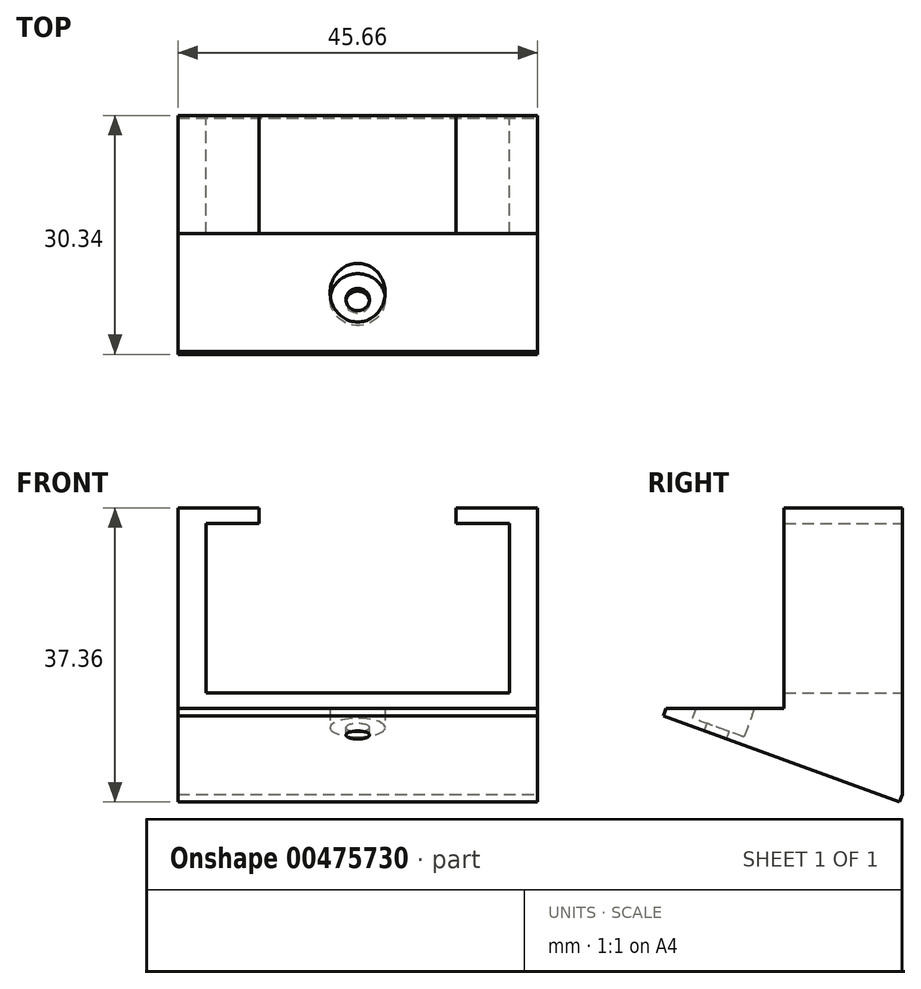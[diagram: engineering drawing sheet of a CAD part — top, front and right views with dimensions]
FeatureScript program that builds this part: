
annotation { "Feature Type Name" : "Feature", "Feature Type Description" : "" }
export const myFeature = defineFeature(function(context is Context, id is Id, definition is map)
    precondition{}
    {
        {
            var Q0;
            Q0=qCreatedBy(makeId("Front.planeOp"),FACE);
            var sketch = newSketch(context, id + "F0", { "sketchPlane" : qUnion([Q0])});
            skLineSegment(sketch, "E0.bottom", {"start": v(-19.25, 0) * mm, "end": v(19.25, 0) * mm});
            skLineSegment(sketch, "E0.top", {"start": v(-19.25, 21.5) * mm, "end": v(19.25, 21.5) * mm});
            skLineSegment(sketch, "E0.left", {"start": v(-19.25, 0) * mm, "end": v(-19.25, 21.5) * mm});
            skLineSegment(sketch, "E0.right", {"start": v(19.25, 0) * mm, "end": v(19.25, 21.5) * mm});
            skLineSegment(sketch, "E1.bottom", {"start": v(-22.83, -2) * mm, "end": v(22.83, -2) * mm});
            skLineSegment(sketch, "E1.top", {"start": v(-22.83, 23.5) * mm, "end": v(22.83, 23.5) * mm});
            skLineSegment(sketch, "E1.left", {"start": v(-22.83, -2) * mm, "end": v(-22.83, 23.5) * mm});
            skLineSegment(sketch, "E1.right", {"start": v(22.83, -2) * mm, "end": v(22.83, 23.5) * mm});
            skLineSegment(sketch, "E2", {"start": v(19.25, 21.5) * mm, "end": v(22.83, 23.5) * mm, "construction": true});
            skLineSegment(sketch, "E3", {"start": v(-19.25, 0) * mm, "end": v(-22.83, -2) * mm, "construction": true});
            skLineSegment(sketch, "E4", {"start": v(-12.5, 23.5) * mm, "end": v(-12.5, 21.5) * mm});
            skLineSegment(sketch, "E5", {"start": v(12.5, 23.5) * mm, "end": v(12.5, 21.5) * mm});
            skSolve(sketch);
        }
        {
            var Q0;
            Q0=makeQuery(id+"F0.imprint","IMPRINT",FACE,{"disambiguationData":[TD([[makeQuery(id+"F0.imprint","IMPRINT",EDGE,{"derivedFrom":sQuery(id+"F0.wireOp",EDGE,"E0.bottom")}),-1.0]])]});
            extrude(context, id + "F1", {"entities" : qUnion([Q0]), "depth" : 15 * mm});
        }
        {
            var Q0;
            Q0=makeQuery(id+"F1.opExtrude","SWEPT_FACE",FACE,{"disambiguationData":[OSD([sQuery(id+"F0.wireOp",EDGE,"E1.right")])]});
            var sketch = newSketch(context, id + "F2", { "sketchPlane" : qUnion([Q0])});
            skLineSegment(sketch, "E6", {"start": v(-30, -2) * mm, "end": v(0, -2) * mm});
            skLineSegment(sketch, "E7", {"start": v(0, -2) * mm, "end": v(0, -12.92) * mm});
            skLineSegment(sketch, "E8", {"start": v(0, -12.92) * mm, "end": v(-30, -2) * mm});
            skSolve(sketch);
        }
        {
            var Q0;
            Q0=qSketchRegion(id+"F2",true);
            var Q1;
            Q1=makeQuery(id+"F1.opExtrude","SWEPT_FACE",FACE,{"disambiguationData":[OSD([sQuery(id+"F0.wireOp",EDGE,"E1.left")])]});
            extrude(context, id + "F3", {"entities" : qUnion([Q0]), "operationType" : NewBodyOperationType.ADD, "endBound" : BoundingType.UP_TO_SURFACE, "oppositeDirection" : true, "endBoundEntityFace" : qUnion([Q1]), "depth" : 25 * mm});
        }
        {
            var Q0;
            Q0=makeQuery(id+"F3.opExtrude","SWEPT_FACE",FACE,{"disambiguationData":[OSD([sQuery(id+"F2.wireOp",EDGE,"E8")])]});
            var sketch = newSketch(context, id + "F4", { "sketchPlane" : qUnion([Q0])});
            skLineSegment(sketch, "E9.0", {"start": v(-22.83, 13.41) * mm, "end": v(22.83, 13.41) * mm});
            skLineSegment(sketch, "E10", {"start": v(-22.83, 13.41) * mm, "end": v(-22.83, 27.5) * mm, "construction": true});
            skCircle(sketch, "E11", {"center": v(0, 20.46) * mm, "radius": 3.5 * mm});
            skPoint(sketch, "E11.centerSnap0", {"position": v(-22.83, 20.46) * mm});
            skPoint(sketch, "E11.centerSnap1", {"position": v(0, 13.41) * mm});
            skSolve(sketch);
        }
        {
            var Q0;
            Q0=qSketchRegion(id+"F4",true);
            extrude(context, id + "F5", {"entities" : qUnion([Q0]), "operationType" : NewBodyOperationType.REMOVE, "endBound" : BoundingType.UP_TO_NEXT, "oppositeDirection" : true, "depth" : 25 * mm});
        }
        {
            var Q0;
            Q0=makeQuery(id+"F3.opExtrude","SWEPT_FACE",FACE,{"disambiguationData":[OSD([sQuery(id+"F2.wireOp",EDGE,"E8")])]});
            var sketch = newSketch(context, id + "F6", { "sketchPlane" : qUnion([Q0])});
            skCircle(sketch, "E12", {"center": v(0, 20.46) * mm, "radius": 1.5 * mm});
            skSolve(sketch);
        }
        {
            var Q0;
            {var subQ0=sQuery(id+"F2.wireOp",EDGE,"E8");Q0=makeQuery(id+"F6.imprint","IMPRINT",FACE,{"disambiguationData":[TD([[makeQuery(id+"F6.imprint","IMPRINT",EDGE,{"derivedFrom":makeQuery(id+"F3.opExtrude","CAP_EDGE",EDGE,{"disambiguationData":[OSD([subQ0])],"isStart":true})}),1.0]])]});}
            var Q1;
            Q1=makeQuery(id+"F6.imprint","IMPRINT",FACE,{"disambiguationData":[TD([[makeQuery(id+"F6.imprint","IMPRINT",EDGE,{"derivedFrom":sQuery(id+"F6.wireOp",EDGE,"E12")}),-1.0]])]});
            extrude(context, id + "F7", {"entities" : qUnion([Q0, Q1]), "operationType" : NewBodyOperationType.ADD, "depth" : 1 * mm});
        }
    });
